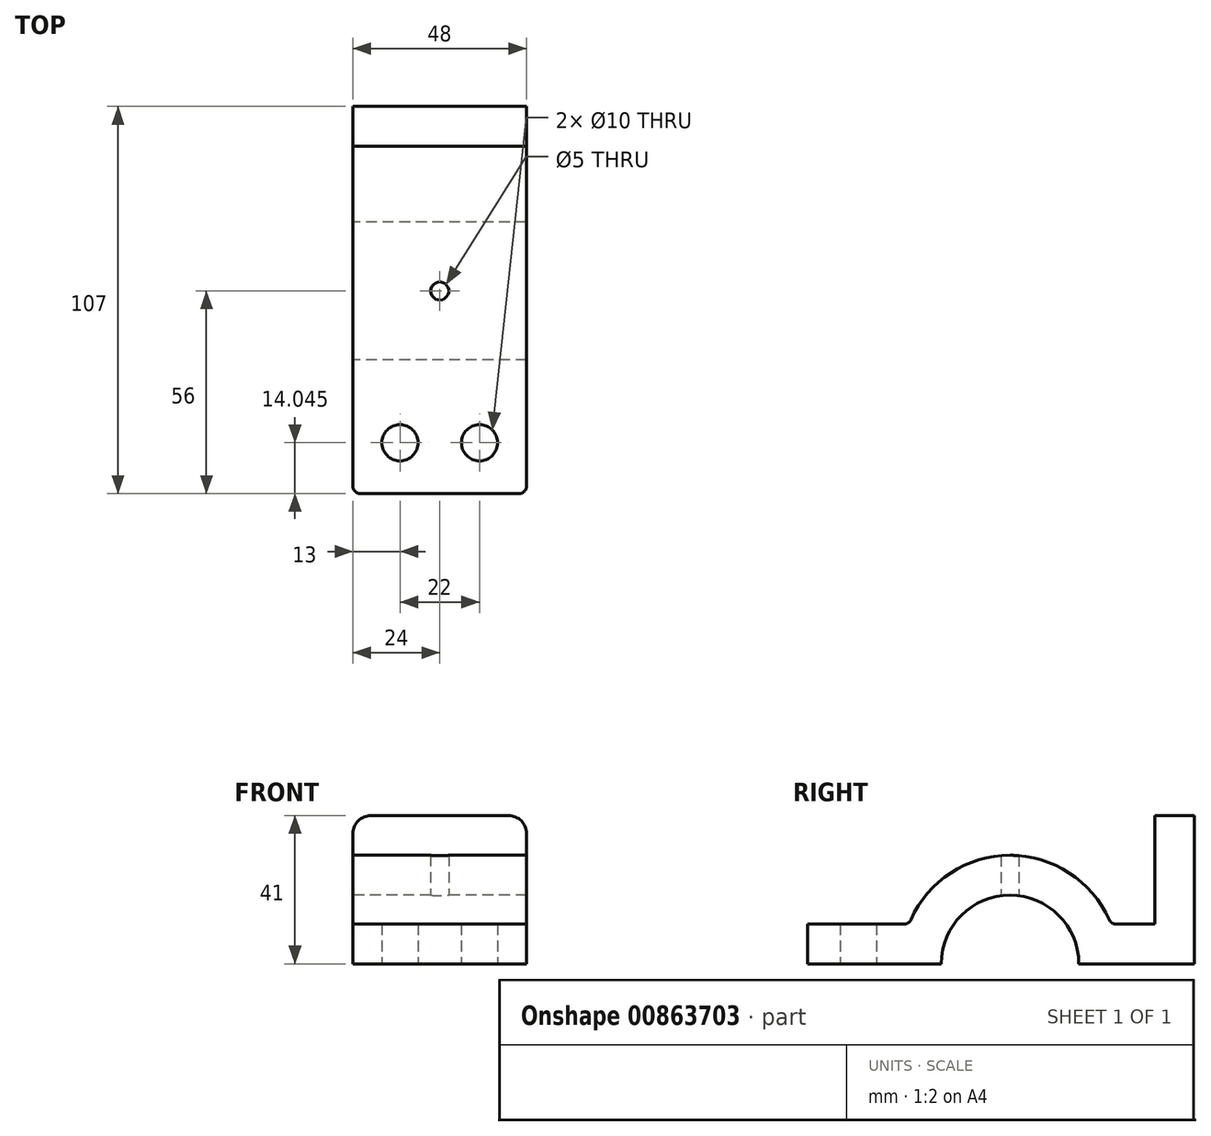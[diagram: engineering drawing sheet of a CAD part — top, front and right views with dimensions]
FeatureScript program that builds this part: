
annotation { "Feature Type Name" : "Feature", "Feature Type Description" : "" }
export const myFeature = defineFeature(function(context is Context, id is Id, definition is map)
    precondition{}
    {
        {
            var Q0;
            Q0=qCreatedBy(makeId("Right.planeOp"),FACE);
            var sketch = newSketch(context, id + "F0", { "sketchPlane" : qUnion([Q0])});
            skCircle(sketch, "E0", {"center": v(0, 0) * mm, "radius": 19 * mm});
            skCircle(sketch, "E1", {"center": v(0, 0) * mm, "radius": 30 * mm});
            skLineSegment(sketch, "E2.bottom", {"start": v(-56, 0) * mm, "end": v(51, 0) * mm});
            skLineSegment(sketch, "E2.top", {"start": v(-56, 11) * mm, "end": v(51, 11) * mm});
            skLineSegment(sketch, "E2.left", {"start": v(-56, 0) * mm, "end": v(-56, 11) * mm});
            skLineSegment(sketch, "E2.right", {"start": v(51, 0) * mm, "end": v(51, 11) * mm});
            skLineSegment(sketch, "E3.bottom", {"start": v(51, 11) * mm, "end": v(40, 11) * mm});
            skLineSegment(sketch, "E3.top", {"start": v(51, 41) * mm, "end": v(40, 41) * mm});
            skLineSegment(sketch, "E3.left", {"start": v(51, 11) * mm, "end": v(51, 41) * mm});
            skLineSegment(sketch, "E3.right", {"start": v(40, 11) * mm, "end": v(40, 41) * mm});
            skLineSegment(sketch, "E4", {"start": v(-56, 11) * mm, "end": v(-85.2, 21.14) * mm});
            skLineSegment(sketch, "E5", {"start": v(-85.2, 21.14) * mm, "end": v(-79.08, -3.53) * mm});
            skLineSegment(sketch, "E6", {"start": v(-79.08, -3.53) * mm, "end": v(-56, 0) * mm});
            skSolve(sketch);
        }
        {
            var Q0;
            {var subQ5=sQuery(id+"F0.wireOp",EDGE,"E2.left");Q0=makeQuery(id+"F0.imprint","IMPRINT",FACE,{"disambiguationData":[TD([[makeQuery(id+"F0.imprint","IMPRINT",EDGE,{"derivedFrom":subQ5}),-1.0]])]});}
            var Q1;
            {var subQ0=sQuery(id+"F0.wireOp",EDGE,"E2.bottom");var subQ1=sQuery(id+"F0.wireOp",EDGE,"E0");var subQ2=makeQuery(id+"F0.imprint","INTERSECT",VERTEX,{"disambiguationData":[OD(0.0)],"derivedFrom":[subQ1,subQ0]});Q1=makeQuery(id+"F0.imprint","IMPRINT",FACE,{"disambiguationData":[TD([[makeQuery(id+"F0.imprint","IMPRINT",EDGE,{"disambiguationData":[TD([[subQ2,1.0]])],"derivedFrom":subQ1}),-1.0]])]});}
            var Q2;
            {var subQ0=sQuery(id+"F0.wireOp",EDGE,"E2.top");var subQ1=sQuery(id+"F0.wireOp",EDGE,"E0");var subQ2=makeQuery(id+"F0.imprint","INTERSECT",VERTEX,{"disambiguationData":[OD(0.0)],"derivedFrom":[subQ1,subQ0]});Q2=makeQuery(id+"F0.imprint","IMPRINT",FACE,{"disambiguationData":[TD([[makeQuery(id+"F0.imprint","IMPRINT",EDGE,{"disambiguationData":[TD([[subQ2,1.0]])],"derivedFrom":subQ1}),-1.0]])]});}
            var Q3;
            {var subQ0=sQuery(id+"F0.wireOp",EDGE,"E2.top");var subQ1=sQuery(id+"F0.wireOp",EDGE,"E0");var subQ2=makeQuery(id+"F0.imprint","INTERSECT",VERTEX,{"disambiguationData":[OD(1.0)],"derivedFrom":[subQ1,subQ0]});Q3=makeQuery(id+"F0.imprint","IMPRINT",FACE,{"disambiguationData":[TD([[makeQuery(id+"F0.imprint","IMPRINT",EDGE,{"disambiguationData":[TD([[subQ2,1.0]])],"derivedFrom":subQ1}),-1.0]])]});}
            var Q4;
            {var subQ0=sQuery(id+"F0.wireOp",EDGE,"E2.right");Q4=makeQuery(id+"F0.imprint","IMPRINT",FACE,{"disambiguationData":[TD([[makeQuery(id+"F0.imprint","IMPRINT",EDGE,{"derivedFrom":subQ0}),1.0]])]});}
            var Q5;
            Q5=makeQuery(id+"F0.imprint","IMPRINT",FACE,{"disambiguationData":[TD([[makeQuery(id+"F0.imprint","IMPRINT",EDGE,{"derivedFrom":sQuery(id+"F0.wireOp",EDGE,"E3.top")}),1.0]])]});
            extrude(context, id + "F1", {"entities" : qUnion([Q0, Q1, Q2, Q3, Q4, Q5]), "endBound" : BoundingType.SYMMETRIC, "depth" : 48 * mm, "offsetDistance" : 25 * mm});
        }
        {
            var Q0;
            Q0=makeQuery(id+"F1.opExtrude","SWEPT_FACE",FACE,{"disambiguationData":[OSD([sQuery(id+"F0.wireOp",EDGE,"E2.right"),sQuery(id+"F0.wireOp",EDGE,"E3.left")])]});
            var sketch = newSketch(context, id + "F2", { "sketchPlane" : qUnion([Q0])});
            skLineSegment(sketch, "E7", {"start": v(0, 0) * mm, "end": v(0, 41) * mm, "construction": true});
            skCircle(sketch, "E8", {"center": v(0, 25) * mm, "radius": 6.5 * mm});
            skLineSegment(sketch, "E9", {"start": v(-6.5, 25) * mm, "end": v(-6.5, 41) * mm});
            skLineSegment(sketch, "E10", {"start": v(6.5, 25) * mm, "end": v(6.5, 41) * mm});
            skSolve(sketch);
        }
        {
            var Q0;
            {var subQ0=sQuery(id+"F2.wireOp",EDGE,"E8");var subQ2=makeQuery(id+"F2.imprint","INTERSECT",VERTEX,{"derivedFrom":[subQ0,sQuery(id+"F2.wireOp",EDGE,"E9")]});Q0=makeQuery(id+"F2.imprint","IMPRINT",FACE,{"disambiguationData":[TD([[makeQuery(id+"F2.imprint","IMPRINT",EDGE,{"disambiguationData":[TD([[subQ2,1.0]])],"derivedFrom":subQ0}),1.0]])]});}
            var Q1;
            {var subQ2=sQuery(id+"F2.wireOp",EDGE,"E9");Q1=makeQuery(id+"F2.imprint","IMPRINT",FACE,{"disambiguationData":[TD([[makeQuery(id+"F2.imprint","IMPRINT",EDGE,{"derivedFrom":subQ2}),-1.0]])]});}
            var Q2;
            Q2=makeQuery(id+"F1.opExtrude","SWEPT_FACE",FACE,{"disambiguationData":[OSD([sQuery(id+"F0.wireOp",EDGE,"E3.right")])]});
            extrude(context, id + "F3", {"entities" : qUnion([Q0, Q1]), "operationType" : NewBodyOperationType.REMOVE, "endBoundEntityFace" : qUnion([Q2]), "offsetDistance" : 25 * mm, "depth" : 25 * mm});
        }
        {
            var Q0;
            Q0=qCreatedBy(makeId("Top.planeOp"),FACE);
            var sketch = newSketch(context, id + "F4", { "sketchPlane" : qUnion([Q0])});
            skCircle(sketch, "E11", {"center": v(0, 0) * mm, "radius": 2.5 * mm});
            skLineSegment(sketch, "E12", {"start": v(24, -41.96) * mm, "end": v(-24, -41.96) * mm, "construction": true});
            skLineSegment(sketch, "E13", {"start": v(0, -56) * mm, "end": v(0, -27.91) * mm, "construction": true});
            skCircle(sketch, "E14", {"center": v(-11, -41.96) * mm, "radius": 5 * mm});
            skCircle(sketch, "E15", {"center": v(11, -41.96) * mm, "radius": 5 * mm});
            skSolve(sketch);
        }
        {
            var Q0;
            Q0=qSketchRegion(id+"F4",true);
            extrude(context, id + "F5", {"entities" : qUnion([Q0]), "operationType" : NewBodyOperationType.REMOVE, "endBound" : BoundingType.THROUGH_ALL, "depth" : 25 * mm});
        }
        {
            var Q0;
            Q0=makeQuery(id+"F1.opExtrude","CAP_EDGE",EDGE,{"disambiguationData":[OSD([sQuery(id+"F0.wireOp",EDGE,"E2.left")])],"isStart":false});
            var Q1;
            Q1=makeQuery(id+"F1.opExtrude","CAP_EDGE",EDGE,{"disambiguationData":[OSD([sQuery(id+"F0.wireOp",EDGE,"E2.left")])],"isStart":true});
            fillet(context, id + "F6", {"entities" : qUnion([Q0, Q1]), "radius" : 2 * mm, "tangentPropagation" : true, "allowEdgeOverflow" : false});
        }
        {
            var Q0;
            Q0=makeQuery(id+"F1.opExtrude","CAP_EDGE",EDGE,{"disambiguationData":[OSD([sQuery(id+"F0.wireOp",EDGE,"E3.top")])],"isStart":false});
            var Q1;
            Q1=makeQuery(id+"F1.opExtrude","CAP_EDGE",EDGE,{"disambiguationData":[OSD([sQuery(id+"F0.wireOp",EDGE,"E3.top")])],"isStart":true});
            fillet(context, id + "F7", {"entities" : qUnion([Q0, Q1]), "radius" : 5 * mm, "tangentPropagation" : true, "allowEdgeOverflow" : false});
        }
        {
            var Q0;
            {var subQ0=sQuery(id+"F0.wireOp",EDGE,"E2.top");var subQ1=sQuery(id+"F0.wireOp",EDGE,"E1");Q0=makeQuery(id+"F1.opExtrude","SWEPT_EDGE",EDGE,{"disambiguationData":[OSD([subQ1,subQ0]),TDD([makeQuery(id+"F0.imprint","INTERSECT",VERTEX,{"disambiguationData":[OD(1.0)],"derivedFrom":[subQ1,subQ0]})])]});}
            var Q1;
            {var subQ0=sQuery(id+"F0.wireOp",EDGE,"E2.top");var subQ1=sQuery(id+"F0.wireOp",EDGE,"E1");Q1=makeQuery(id+"F1.opExtrude","SWEPT_EDGE",EDGE,{"disambiguationData":[OSD([subQ1,subQ0]),TDD([makeQuery(id+"F0.imprint","INTERSECT",VERTEX,{"disambiguationData":[OD(0.0)],"derivedFrom":[subQ1,subQ0]})])]});}
            fillet(context, id + "F8", {"entities" : qUnion([Q0, Q1]), "radius" : 2 * mm, "tangentPropagation" : true, "allowEdgeOverflow" : false});
        }
    });
